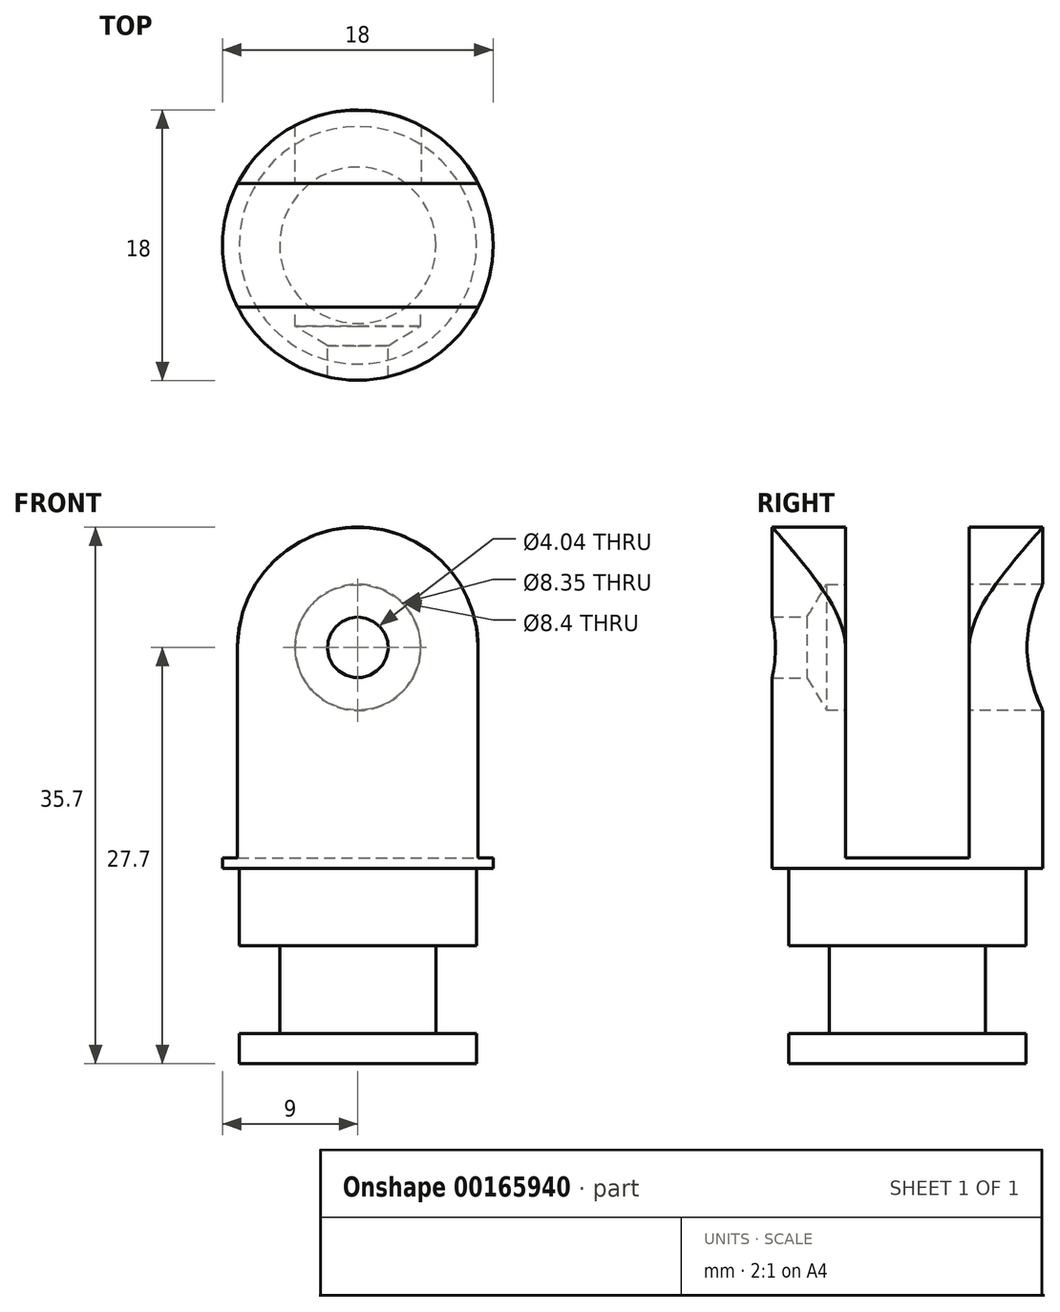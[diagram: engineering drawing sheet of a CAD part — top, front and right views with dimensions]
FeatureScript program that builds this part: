
annotation { "Feature Type Name" : "Feature", "Feature Type Description" : "" }
export const myFeature = defineFeature(function(context is Context, id is Id, definition is map)
    precondition{}
    {
        {
            var Q0;
            Q0=qCreatedBy(makeId("Front.planeOp"),FACE);
            var sketch = newSketch(context, id + "F0", { "sketchPlane" : qUnion([Q0])});
            skLineSegment(sketch, "E0", {"start": v(0, 0) * mm, "end": v(9, 0) * mm});
            skLineSegment(sketch, "E1", {"start": v(9, 0) * mm, "end": v(9, -22.7) * mm});
            skLineSegment(sketch, "E2", {"start": v(9, -22.7) * mm, "end": v(7.9, -22.7) * mm});
            skLineSegment(sketch, "E3", {"start": v(7.9, -22.7) * mm, "end": v(7.9, -27.85) * mm});
            skLineSegment(sketch, "E4", {"start": v(7.9, -27.85) * mm, "end": v(5.2, -27.85) * mm});
            skLineSegment(sketch, "E5", {"start": v(5.2, -27.85) * mm, "end": v(5.2, -33.7) * mm});
            skLineSegment(sketch, "E6", {"start": v(5.2, -33.7) * mm, "end": v(7.9, -33.7) * mm});
            skLineSegment(sketch, "E7", {"start": v(7.9, -33.7) * mm, "end": v(7.9, -35.7) * mm});
            skLineSegment(sketch, "E8", {"start": v(7.9, -35.7) * mm, "end": v(0, -35.7) * mm});
            skLineSegment(sketch, "E9", {"start": v(0, -35.7) * mm, "end": v(0, 0) * mm});
            skSolve(sketch);
        }
        {
            var Q0;
            Q0 = qSketchRegion(id + "F0", true);
            var Q1;
            Q1=sQuery(id+"F0.wireOp",EDGE,"E9");
            revolve(context, id + "F1", {"entities" : qUnion([Q0]), "axis" : qUnion([Q1]), "revolveType" : RevolveType.FULL});
        }
        {
            var Q0;
            Q0=qCreatedBy(makeId("Right.planeOp"),FACE);
            var sketch = newSketch(context, id + "F2", { "sketchPlane" : qUnion([Q0])});
            skLineSegment(sketch, "E10.bottom", {"start": v(4.12, 0) * mm, "end": v(-4.12, 0) * mm});
            skLineSegment(sketch, "E10.top", {"start": v(4.12, -22) * mm, "end": v(-4.12, -22) * mm});
            skLineSegment(sketch, "E10.left", {"start": v(4.12, 0) * mm, "end": v(4.12, -22) * mm});
            skLineSegment(sketch, "E10.right", {"start": v(-4.12, 0) * mm, "end": v(-4.12, -22) * mm});
            skLineSegment(sketch, "E11", {"start": v(0, 0) * mm, "end": v(0, -23.52) * mm, "construction": true});
            skSolve(sketch);
        }
        {
            var Q0;
            Q0 = qSketchRegion(id + "F2", true);
            extrude(context, id + "F3", {"entities" : qUnion([Q0]), "operationType" : NewBodyOperationType.REMOVE, "endBound" : BoundingType.THROUGH_ALL, "oppositeDirection" : true, "depth" : 25 * mm, "hasSecondDirection" : true, "secondDirectionBound" : SecondDirectionBoundingType.THROUGH_ALL, "secondDirectionOppositeDirection" : false, "secondDirectionDepth" : 25 * mm});
        }
        {
            var Q0;
            Q0=makeQuery(id+"F3.boolean.opBoolean","COPY",FACE,{"derivedFrom":makeQuery(id+"F3.opExtrude","SWEPT_FACE",FACE,{"disambiguationData":[OSD([sQuery(id+"F2.wireOp",EDGE,"E10.right")])]})});
            var sketch = newSketch(context, id + "F4", { "sketchPlane" : qUnion([Q0])});
            skPoint(sketch, "E12", {"position": v(0, -8) * mm});
            skSolve(sketch);
        }
        {
            var Q0;
            Q0=sQuery(id+"F4.wireOp",VERTEX,"E12");
            var Q1;
            Q1=makeQuery(id+"F1.opRevolve","SWEPT_BODY",BODY,{"disambiguationData":[OSD([sQuery(id+"F0.wireOp",EDGE,"E0"),sQuery(id+"F0.wireOp",EDGE,"E1"),sQuery(id+"F0.wireOp",EDGE,"E2"),sQuery(id+"F0.wireOp",EDGE,"E3"),sQuery(id+"F0.wireOp",EDGE,"E4"),sQuery(id+"F0.wireOp",EDGE,"E5"),sQuery(id+"F0.wireOp",EDGE,"E6"),sQuery(id+"F0.wireOp",EDGE,"E7"),sQuery(id+"F0.wireOp",EDGE,"E8"),sQuery(id+"F0.wireOp",EDGE,"E9")])]});
            hole(context, id + "F5", {"style" : HoleStyle.SIMPLE, "endStyle" : HoleEndStyle.THROUGH, "standardTappedOrClearance" : lookupTablePath({ "standard" : "ANSI", "engagement" : "75%", "pitch" : "32 tpi", "size" : "#10", "type" : "Tapped" }), "standardBlindInLast" : lookupTablePath({ "standard" : "ANSI", "engagement" : "75%", "pitch" : "32 tpi", "size" : "#10", "type" : "Tapped" }), "holeDiameter" : 4.04 * mm, "locations" : qUnion([Q0]), "scope" : qUnion([Q1]), "isTappedThrough" : true, "majorDiameter" : 4.83 * mm, "showTappedDepth" : true});
        }
        {
            var Q0;
            Q0=sQuery(id+"F4.wireOp",VERTEX,"E12");
            var Q1;
            Q1=makeQuery(id+"F1.opRevolve","SWEPT_BODY",BODY,{"disambiguationData":[OSD([sQuery(id+"F0.wireOp",EDGE,"E0"),sQuery(id+"F0.wireOp",EDGE,"E1"),sQuery(id+"F0.wireOp",EDGE,"E2"),sQuery(id+"F0.wireOp",EDGE,"E3"),sQuery(id+"F0.wireOp",EDGE,"E4"),sQuery(id+"F0.wireOp",EDGE,"E5"),sQuery(id+"F0.wireOp",EDGE,"E6"),sQuery(id+"F0.wireOp",EDGE,"E7"),sQuery(id+"F0.wireOp",EDGE,"E8"),sQuery(id+"F0.wireOp",EDGE,"E9")])]});
            hole(context, id + "F6", {"style" : HoleStyle.SIMPLE, "endStyle" : HoleEndStyle.BLIND, "holeDiameter" : 8.35 * mm, "holeDepth" : 1.25 * mm, "locations" : qUnion([Q0]), "scope" : qUnion([Q1])});
        }
        {
            var Q0;
            Q0=makeQuery(id+"F3.boolean.opBoolean","COPY",FACE,{"derivedFrom":makeQuery(id+"F3.opExtrude","SWEPT_FACE",FACE,{"disambiguationData":[OSD([sQuery(id+"F2.wireOp",EDGE,"E10.left")])]})});
            var sketch = newSketch(context, id + "F7", { "sketchPlane" : qUnion([Q0])});
            skPoint(sketch, "E13", {"position": v(0, -8) * mm});
            skSolve(sketch);
        }
        {
            var Q0;
            Q0=sQuery(id+"F7.wireOp",VERTEX,"E13");
            var Q1;
            Q1=makeQuery(id+"F1.opRevolve","SWEPT_BODY",BODY,{"disambiguationData":[OSD([sQuery(id+"F0.wireOp",EDGE,"E0"),sQuery(id+"F0.wireOp",EDGE,"E1"),sQuery(id+"F0.wireOp",EDGE,"E2"),sQuery(id+"F0.wireOp",EDGE,"E3"),sQuery(id+"F0.wireOp",EDGE,"E4"),sQuery(id+"F0.wireOp",EDGE,"E5"),sQuery(id+"F0.wireOp",EDGE,"E6"),sQuery(id+"F0.wireOp",EDGE,"E7"),sQuery(id+"F0.wireOp",EDGE,"E8"),sQuery(id+"F0.wireOp",EDGE,"E9")])]});
            hole(context, id + "F8", {"style" : HoleStyle.SIMPLE, "endStyle" : HoleEndStyle.THROUGH, "holeDiameter" : 8.4 * mm, "locations" : qUnion([Q0]), "scope" : qUnion([Q1]), "isTappedThrough" : true});
        }
        {
            var Q0;
            Q0=qCreatedBy(makeId("Front.planeOp"),FACE);
            var sketch = newSketch(context, id + "F9", { "sketchPlane" : qUnion([Q0])});
            skCircle(sketch, "E14.0", {"center": v(0, -8) * mm, "radius": 4.2 * mm, "construction": true});
            skArc(sketch, "E15", {"start": v(8, -8) * mm, "mid": v(0, 0) * mm, "end": v(-8, -8) * mm});
            skLineSegment(sketch, "E16", {"start": v(8, -8) * mm, "end": v(8, 2.46) * mm});
            skLineSegment(sketch, "E17", {"start": v(8, 2.46) * mm, "end": v(-8, 2.46) * mm});
            skLineSegment(sketch, "E18", {"start": v(-8, 2.46) * mm, "end": v(-8, -8) * mm});
            skSolve(sketch);
        }
        {
            var Q0;
            Q0 = qSketchRegion(id + "F9", true);
            extrude(context, id + "F10", {"entities" : qUnion([Q0]), "operationType" : NewBodyOperationType.REMOVE, "endBound" : BoundingType.THROUGH_ALL, "oppositeDirection" : true, "depth" : 25 * mm, "hasSecondDirection" : true, "secondDirectionBound" : SecondDirectionBoundingType.THROUGH_ALL, "secondDirectionOppositeDirection" : false, "secondDirectionDepth" : 25 * mm});
        }
    });
